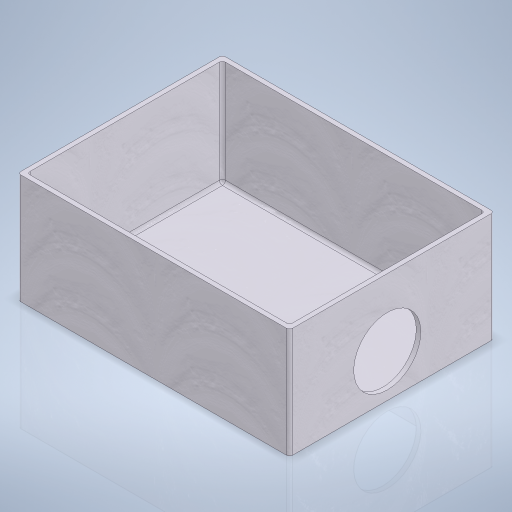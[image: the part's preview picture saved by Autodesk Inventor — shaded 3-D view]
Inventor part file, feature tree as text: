
AUTODESK INVENTOR PART (.ipt)
format: ipt  version: 2024 (Build 280153000, 153)  size: 335,872 bytes
history: native  units: mm
features: extrude x2, sketch x2, shell x1, fillet x1
ambient origin geometry x8: Origin, YZ Plane, XZ Plane, XY Plane, X Axis, Y Axis, Z Axis, Center Point
bodies: Volumenkörper1 (feature_tree)
feature tree (6):
  extrude  "Extrusion1"  Depth=67.0mm
  shell  "Wandung1"  Thickness=36.0mm
  extrude  "Extrusion2"  Depth=1.0mm
  fillet  "Rundung1"  Radius=14.0mm
  sketch  "Skizze2"  dims[d0=89.0mm d1=67.0mm d2=36.0mm d3=0.0mm]
  sketch  "Skizze3"  dims[d4=1.5mm d5=22.0mm d6=14.0mm d7=35.0mm d8=36.0mm d9=0.0mm d10=1.0mm]
